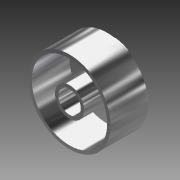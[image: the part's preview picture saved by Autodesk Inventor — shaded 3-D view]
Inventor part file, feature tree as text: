
AUTODESK INVENTOR PART (.ipt)
format: ipt  version: 2015 (Build 190159000, 159)  size: 149,504 bytes
history: native  units: in
note: dims shown in document units (in); Inventor stores cm internally (conversion verified against a paired STEP export)
features: extrude x3, sketch x3, projected_geometry x2, plane x1
ambient origin geometry x8: Origin, YZ Plane, XZ Plane, XY Plane, X Axis, Y Axis, Z Axis, Center Point
bodies: Solid1 (feature_tree)
feature tree (9):
  extrude  "Extrusion1"  TaperAngle=0.0deg  [1 undecoded]
  plane  "Work Plane1"
  extrude  "Extrusion2"  Depth=0.05in
  extrude  "Extrusion3"  Depth=0.05in TaperAngle=0.0deg
  sketch  "Sketch1"  dims[d5=0.57in d6=0.0in d10=0.0in]
  sketch  "Sketch4"  dims[d11=0.05in d12=0.0in d13=0.5in]
  projected_geometry  "Projected Loop3"
  projected_geometry  "Projected Loop4"
  sketch  "Sketch5"  dims[d14=1.9685in d16=360.0deg d18=0.05in d19=0.0in d20=0.05in d21=0.35in d22=0.44in d23=0.05in d24=0.25in]
note: 1 required parameter value undecoded (feature->parameter linkage not recoverable at this tier; creation-order binding heuristic only, values carry confidence <= 0.55)
